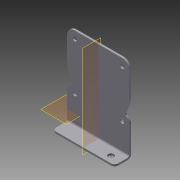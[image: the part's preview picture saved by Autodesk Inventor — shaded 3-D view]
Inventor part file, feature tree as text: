
AUTODESK INVENTOR PART (.ipt)
format: ipt  version: 2016 SP1 (Build 200210100, 210)  size: 172,544 bytes
history: native  units: in
note: dims shown in document units (in); Inventor stores cm internally (conversion verified against a paired STEP export)
features: sketch x6, extrude x4, fillet x3, hole x2, reference x2, plane x1, mirror x1
ambient origin geometry x8: Origin, YZ Plane, XZ Plane, XY Plane, X Axis, Y Axis, Z Axis, Center Point
bodies: Solid1 (feature_tree)
feature tree (19):
  extrude  "Extrusion1"  Depth=2.11in
  extrude  "Extrusion5"  Depth=2.11in
  extrude  "Extrusion2"  Depth=0.5in TaperAngle=0.0deg
  extrude  "Extrusion4"  Depth=0.25in TaperAngle=0.0deg
  hole  "Hole3"  [1 undecoded]
  plane  "Work Plane1"
  fillet  "Fillet3"  Radius=0.063in
  fillet  "Fillet4"  Radius=0.125in
  fillet  "Fillet5"  Radius=0.125in
  hole  "Hole6"  [1 undecoded]
  mirror  "Mirror1"
  sketch  "Sketch1"  dims[d0=2.11in d1=2.5in]
  sketch  "Sketch2"  dims[d2=0.0625in d3=0.0in d4=2.11in]
  sketch  "Sketch6"  dims[d6=0.5in d7=0.0in d29=1.0in d30=0.0in]
  reference  "Reference2"
  sketch  "Sketch7"  dims[d31=0.15in d32=0.75in d33=0.279in d34=0.25in d35=0.5635in d36=1.0in d37=0.8108in d57=1.0in d58=0.0in]
  sketch  "Sketch9"  dims[d59=0.063in d60=2.856in d61=0.063in d62=0.125in d63=0.125in]
  sketch  "Sketch10"  dims[d64=0.201in d65=0.75in d66=0.385in d67=0.25in d68=0.5635in d69=1.0in d70=0.8108in]
  reference  "Reference3"
note: 2 required parameter values undecoded (feature->parameter linkage not recoverable at this tier; creation-order binding heuristic only, values carry confidence <= 0.55)
